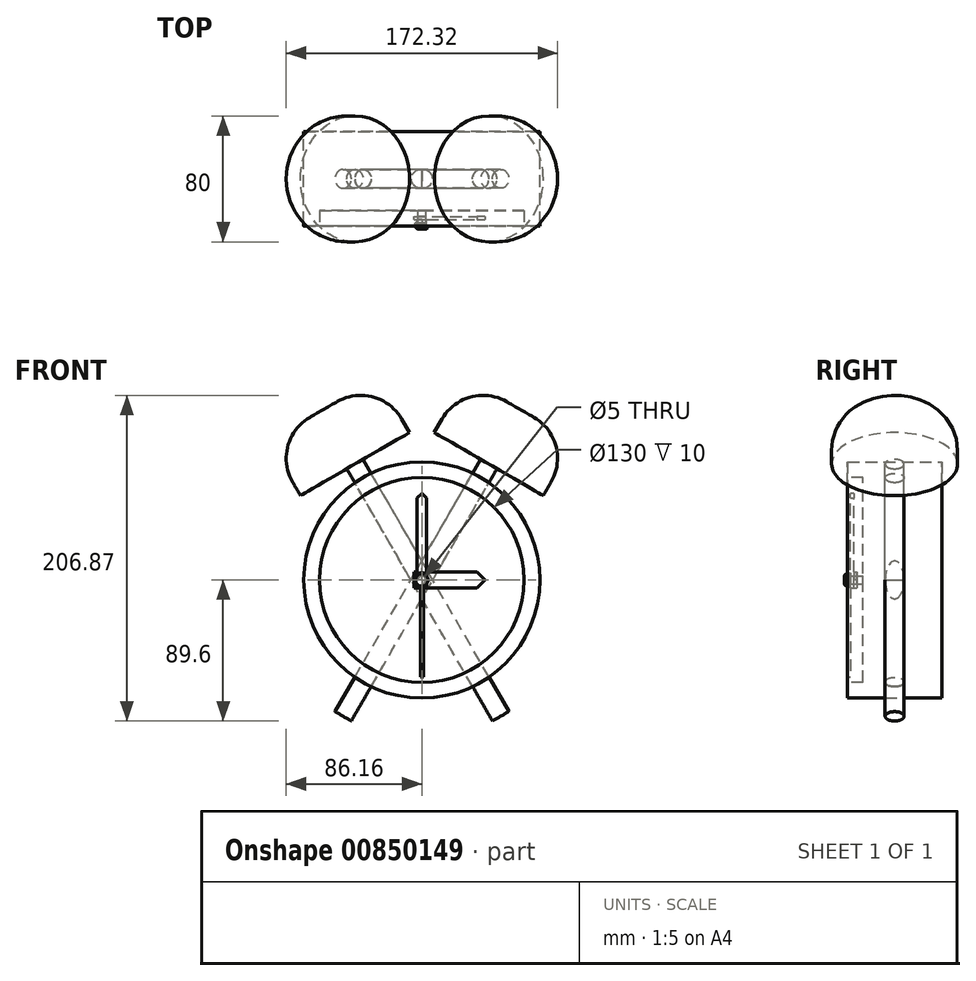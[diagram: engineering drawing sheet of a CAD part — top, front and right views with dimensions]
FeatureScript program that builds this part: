
annotation { "Feature Type Name" : "Feature", "Feature Type Description" : "" }
export const myFeature = defineFeature(function(context is Context, id is Id, definition is map)
    precondition{}
    {
        {
            var Q0;
            Q0=qCreatedBy(makeId("Front.planeOp"),FACE);
            var sketch = newSketch(context, id + "F0", { "sketchPlane" : qUnion([Q0])});
            skCircle(sketch, "E0", {"center": v(0, 0) * mm, "radius": 75 * mm});
            skSolve(sketch);
        }
        {
            var Q0;
            Q0=makeQuery(id+"F0.imprint","IMPRINT",FACE,{"disambiguationData":[TD([[makeQuery(id+"F0.imprint","IMPRINT",EDGE,{"derivedFrom":sQuery(id+"F0.wireOp",EDGE,"E0")}),1.0]])]});
            extrude(context, id + "F1", {"entities" : qUnion([Q0]), "depth" : 60 * mm, "offsetDistance" : 25 * mm});
        }
        {
            var Q0;
            Q0=makeQuery(id+"F1.opExtrude","CAP_FACE",FACE,{"disambiguationData":[OSD([sQuery(id+"F0.wireOp",EDGE,"E0")])],"isStart":false});
            var sketch = newSketch(context, id + "F2", { "sketchPlane" : qUnion([Q0])});
            skCircle(sketch, "E1", {"center": v(0, 0) * mm, "radius": 65 * mm});
            skSolve(sketch);
        }
        {
            var Q0;
            Q0=makeQuery(id+"F2.imprint","IMPRINT",FACE,{"disambiguationData":[TD([[makeQuery(id+"F2.imprint","IMPRINT",EDGE,{"derivedFrom":sQuery(id+"F2.wireOp",EDGE,"E1")}),1.0]])]});
            extrude(context, id + "F3", {"entities" : qUnion([Q0]), "operationType" : NewBodyOperationType.REMOVE, "oppositeDirection" : true, "depth" : 10 * mm, "offsetDistance" : 25 * mm});
        }
        {
            var Q0;
            Q0=qCreatedBy(makeId("Front.planeOp"),FACE);
            var sketch = newSketch(context, id + "F4", { "sketchPlane" : qUnion([Q0])});
            skLineSegment(sketch, "E2", {"start": v(0, 125) * mm, "end": v(0, -100) * mm});
            skLineSegment(sketch, "E3", {"start": v(0, 125) * mm, "end": v(40, 125) * mm});
            skLineSegment(sketch, "E4", {"start": v(6, -100) * mm, "end": v(0, -100) * mm});
            skLineSegment(sketch, "E5", {"start": v(40, 125) * mm, "end": v(40, 85) * mm});
            skLineSegment(sketch, "E6", {"start": v(40, 85) * mm, "end": v(6, 85) * mm});
            skLineSegment(sketch, "E7", {"start": v(6, -100) * mm, "end": v(6, 85) * mm});
            skSolve(sketch);
        }
        {
            var Q0;
            Q0 = qSketchRegion(id + "F4", true);
            var Q1;
            Q1=sQuery(id+"F4.wireOp",EDGE,"E2");
            revolve(context, id + "F5", {"surfaceOperationType" : NewSurfaceOperationType.NEW, "entities" : qUnion([Q0]), "axis" : qUnion([Q1]), "revolveType" : RevolveType.FULL});
        }
        {
            var Q0;
            Q0=makeQuery(id+"F5.opRevolve","SWEPT_EDGE",EDGE,{"disambiguationData":[OSD([sQuery(id+"F4.wireOp",EDGE,"E3"),sQuery(id+"F4.wireOp",EDGE,"E5")])]});
            fillet(context, id + "F6", {"entities" : qUnion([Q0]), "radius" : 30 * mm, "tangentPropagation" : true, "allowEdgeOverflow" : false});
        }
        {
            var Q0;
            Q0=makeQuery(id+"F5.opRevolve","SWEPT_BODY",BODY,{"disambiguationData":[OSD([sQuery(id+"F4.wireOp",EDGE,"E2"),sQuery(id+"F4.wireOp",EDGE,"E3"),sQuery(id+"F4.wireOp",EDGE,"E4"),sQuery(id+"F4.wireOp",EDGE,"E5"),sQuery(id+"F4.wireOp",EDGE,"E6"),sQuery(id+"F4.wireOp",EDGE,"E7")])]});
            var Q1;
            Q1=sQuery(id+"F0.wireOp",EDGE,"E0");
            transform(context, id + "F7", {"entities" : qUnion([Q0]), "transformType" : TransformType.ROTATION, "transformAxis" : qUnion([Q1]), "angle" : 30 * degree, "oppositeDirection" : true, "makeCopy" : false});
        }
        {
            var Q0;
            Q0=makeQuery(id+"F5.opRevolve","SWEPT_BODY",BODY,{"disambiguationData":[OSD([sQuery(id+"F4.wireOp",EDGE,"E2"),sQuery(id+"F4.wireOp",EDGE,"E3"),sQuery(id+"F4.wireOp",EDGE,"E4"),sQuery(id+"F4.wireOp",EDGE,"E5"),sQuery(id+"F4.wireOp",EDGE,"E6"),sQuery(id+"F4.wireOp",EDGE,"E7")])]});
            transform(context, id + "F8", {"entities" : qUnion([Q0]), "transformType" : TransformType.TRANSLATION_3D, "dx" : 0 * mm, "dy" : -30 * mm, "dz" : 0 * mm, "makeCopy" : false});
        }
        {
            var Q0;
            Q0=makeQuery(id+"F5.opRevolve","SWEPT_BODY",BODY,{"disambiguationData":[OSD([sQuery(id+"F4.wireOp",EDGE,"E2"),sQuery(id+"F4.wireOp",EDGE,"E3"),sQuery(id+"F4.wireOp",EDGE,"E4"),sQuery(id+"F4.wireOp",EDGE,"E5"),sQuery(id+"F4.wireOp",EDGE,"E6"),sQuery(id+"F4.wireOp",EDGE,"E7")])]});
            var Q1;
            Q1=qCreatedBy(makeId("Right.planeOp"),FACE);
            mirror(context, id + "F9", {"entities" : qUnion([Q0]), "mirrorPlane" : qUnion([Q1])});
        }
        {
            var Q0;
            Q0=makeQuery(id+"F5.opRevolve","SWEPT_BODY",BODY,{"disambiguationData":[OSD([sQuery(id+"F4.wireOp",EDGE,"E2"),sQuery(id+"F4.wireOp",EDGE,"E3"),sQuery(id+"F4.wireOp",EDGE,"E4"),sQuery(id+"F4.wireOp",EDGE,"E5"),sQuery(id+"F4.wireOp",EDGE,"E6"),sQuery(id+"F4.wireOp",EDGE,"E7")])]});
            var Q1;
            Q1=makeQuery(id+"F9.opPattern","COPY",BODY,{"derivedFrom":makeQuery(id+"F5.opRevolve","SWEPT_BODY",BODY,{"disambiguationData":[OSD([sQuery(id+"F4.wireOp",EDGE,"E2"),sQuery(id+"F4.wireOp",EDGE,"E3"),sQuery(id+"F4.wireOp",EDGE,"E4"),sQuery(id+"F4.wireOp",EDGE,"E5"),sQuery(id+"F4.wireOp",EDGE,"E6"),sQuery(id+"F4.wireOp",EDGE,"E7")])]}),"instanceName":"1"});
            var Q2;
            Q2=makeQuery(id+"F1.opExtrude","SWEPT_BODY",BODY,{"disambiguationData":[OSD([sQuery(id+"F0.wireOp",EDGE,"E0")])]});
            booleanBodies(context, id + "F10", {"operationType" : BooleanOperationType.SUBTRACTION, "tools" : qUnion([Q0, Q1]), "targets" : qUnion([Q2]), "keepTools" : true});
        }
        {
            var Q0;
            Q0=makeQuery(id+"F3.boolean.opBoolean","COPY",FACE,{"derivedFrom":makeQuery(id+"F3.opExtrude","CAP_FACE",FACE,{"disambiguationData":[OSD([sQuery(id+"F2.wireOp",EDGE,"E1")])],"isStart":false})});
            var sketch = newSketch(context, id + "F11", { "sketchPlane" : qUnion([Q0])});
            skCircle(sketch, "E8", {"center": v(0, 0) * mm, "radius": 2.5 * mm});
            skSolve(sketch);
        }
        {
            var Q0;
            Q0=makeQuery(id+"F11.imprint","IMPRINT",FACE,{"disambiguationData":[TD([[makeQuery(id+"F11.imprint","IMPRINT",EDGE,{"derivedFrom":sQuery(id+"F11.wireOp",EDGE,"E8")}),1.0]])]});
            var Q1;
            Q1=sQuery(id+"F11.wireOp",EDGE,"E8");
            extrude(context, id + "F12", {"entities" : qUnion([Q0]), "operationType" : NewBodyOperationType.ADD, "surfaceEntities" : qUnion([Q1]), "depth" : 4 * mm, "offsetDistance" : 25 * mm});
        }
        {
            var Q0;
            Q0=makeQuery(id+"F12.opExtrude","CAP_FACE",FACE,{"disambiguationData":[OSD([sQuery(id+"F11.wireOp",EDGE,"E8")])],"isStart":false});
            var sketch = newSketch(context, id + "F13", { "sketchPlane" : qUnion([Q0])});
            skLineSegment(sketch, "E9.bottom", {"start": v(-5, 5) * mm, "end": v(40, 5) * mm});
            skLineSegment(sketch, "E9.top", {"start": v(-5, -5) * mm, "end": v(40, -5) * mm});
            skLineSegment(sketch, "E9.left", {"start": v(-5, 5) * mm, "end": v(-5, -5) * mm});
            skLineSegment(sketch, "E9.right", {"start": v(40, 5) * mm, "end": v(40, -5) * mm});
            skLineSegment(sketch, "E10", {"start": v(0, 0) * mm, "end": v(-5, 0) * mm});
            skSolve(sketch);
        }
        {
            var Q0;
            {var subQ3=sQuery(id+"F13.wireOp",EDGE,"E9.bottom");Q0=makeQuery(id+"F13.imprint","IMPRINT",FACE,{"disambiguationData":[TD([[makeQuery(id+"F13.imprint","IMPRINT",EDGE,{"derivedFrom":subQ3}),-1.0]])]});}
            extrude(context, id + "F14", {"entities" : qUnion([Q0]), "depth" : 2 * mm, "offsetDistance" : 25 * mm});
        }
        {
            var Q0;
            Q0=makeQuery(id+"F14.opExtrude","SWEPT_EDGE",EDGE,{"disambiguationData":[OSD([sQuery(id+"F13.wireOp",EDGE,"E9.bottom"),sQuery(id+"F13.wireOp",EDGE,"E9.right")])]});
            var Q1;
            Q1=makeQuery(id+"F14.opExtrude","SWEPT_EDGE",EDGE,{"disambiguationData":[OSD([sQuery(id+"F13.wireOp",EDGE,"E9.top"),sQuery(id+"F13.wireOp",EDGE,"E9.right")])]});
            chamfer(context, id + "F15", {"entities" : qUnion([Q0, Q1]), "width" : 5 * mm, "tangentPropagation" : true});
        }
        {
            var Q0;
            Q0=makeQuery(id+"F14.opExtrude","CAP_FACE",FACE,{"disambiguationData":[OSD([sQuery(id+"F11.wireOp",EDGE,"E8"),sQuery(id+"F13.wireOp",EDGE,"E9.bottom"),sQuery(id+"F13.wireOp",EDGE,"E9.top"),sQuery(id+"F13.wireOp",EDGE,"E9.left"),sQuery(id+"F13.wireOp",EDGE,"E9.right")])],"isStart":false});
            var sketch = newSketch(context, id + "F16", { "sketchPlane" : qUnion([Q0])});
            skLineSegment(sketch, "E11.bottom", {"start": v(-3, -5) * mm, "end": v(3, -5) * mm});
            skLineSegment(sketch, "E11.top", {"start": v(-3, 55) * mm, "end": v(3, 55) * mm});
            skLineSegment(sketch, "E11.left", {"start": v(-3, -5) * mm, "end": v(-3, 55) * mm});
            skLineSegment(sketch, "E11.right", {"start": v(3, -5) * mm, "end": v(3, 55) * mm});
            skLineSegment(sketch, "E12", {"start": v(0, 0) * mm, "end": v(0, -5) * mm});
            skSolve(sketch);
        }
        {
            var Q0;
            {var subQ0=sQuery(id+"F16.wireOp",EDGE,"E11.top");Q0=makeQuery(id+"F16.imprint","IMPRINT",FACE,{"disambiguationData":[TD([[makeQuery(id+"F16.imprint","IMPRINT",EDGE,{"derivedFrom":subQ0}),-1.0]])]});}
            var Q1;
            Q1=makeQuery(id+"F16.imprint","IMPRINT",FACE,{"disambiguationData":[TD([[makeQuery(id+"F16.imprint","IMPRINT",EDGE,{"derivedFrom":makeQuery(id+"F14.opExtrude","CAP_EDGE",EDGE,{"disambiguationData":[OSD([sQuery(id+"F11.wireOp",EDGE,"E8")])],"isStart":false})}),-1.0]])]});
            extrude(context, id + "F17", {"entities" : qUnion([Q0, Q1]), "operationType" : NewBodyOperationType.ADD, "depth" : 2 * mm, "offsetDistance" : 25 * mm});
        }
        {
            var Q0;
            Q0=makeQuery(id+"F17.opExtrude","SWEPT_EDGE",EDGE,{"disambiguationData":[OSD([sQuery(id+"F16.wireOp",EDGE,"E11.top"),sQuery(id+"F16.wireOp",EDGE,"E11.right")])]});
            var Q1;
            Q1=makeQuery(id+"F17.opExtrude","SWEPT_EDGE",EDGE,{"disambiguationData":[OSD([sQuery(id+"F16.wireOp",EDGE,"E11.top"),sQuery(id+"F16.wireOp",EDGE,"E11.left")])]});
            chamfer(context, id + "F18", {"entities" : qUnion([Q0, Q1]), "width" : 3 * mm, "tangentPropagation" : true});
        }
        {
            var Q0;
            Q0=makeQuery(id+"F17.opExtrude","CAP_FACE",FACE,{"disambiguationData":[OSD([sQuery(id+"F11.wireOp",EDGE,"E8"),sQuery(id+"F16.wireOp",EDGE,"E11.bottom"),sQuery(id+"F16.wireOp",EDGE,"E11.top"),sQuery(id+"F16.wireOp",EDGE,"E11.left"),sQuery(id+"F16.wireOp",EDGE,"E11.right")])],"isStart":false});
            var sketch = newSketch(context, id + "F19", { "sketchPlane" : qUnion([Q0])});
            skCircle(sketch, "E13", {"center": v(0, 0) * mm, "radius": 4.5 * mm});
            skLineSegment(sketch, "E14.bottom", {"start": v(-1, -1.5) * mm, "end": v(1, -1.5) * mm});
            skLineSegment(sketch, "E14.top", {"start": v(-1, -61.5) * mm, "end": v(1, -61.5) * mm});
            skLineSegment(sketch, "E14.left", {"start": v(1, -1.5) * mm, "end": v(1, -61.5) * mm});
            skLineSegment(sketch, "E14.right", {"start": v(-1, -1.5) * mm, "end": v(-1, -61.5) * mm});
            skLineSegment(sketch, "E15", {"start": v(0, -1.5) * mm, "end": v(0, 0) * mm});
            skSolve(sketch);
        }
        {
            var Q0;
            {var subQ1=sQuery(id+"F19.wireOp",EDGE,"E13");var subQ7=makeQuery(id+"F17.opExtrude","CAP_EDGE",EDGE,{"disambiguationData":[OSD([sQuery(id+"F16.wireOp",EDGE,"E11.left")])],"isStart":false});var subQ9=makeQuery(id+"F19.imprint","INTERSECT",VERTEX,{"disambiguationData":[OD(0.0)],"derivedFrom":[subQ7,subQ1]});Q0=makeQuery(id+"F19.imprint","IMPRINT",FACE,{"disambiguationData":[TD([[makeQuery(id+"F19.imprint","IMPRINT",EDGE,{"disambiguationData":[TD([[subQ9,1.0]])],"derivedFrom":subQ1}),1.0]])]});}
            var Q1;
            {var subQ0=sQuery(id+"F19.wireOp",EDGE,"E13");var subQ1=makeQuery(id+"F17.opExtrude","CAP_EDGE",EDGE,{"disambiguationData":[OSD([sQuery(id+"F16.wireOp",EDGE,"E11.right")])],"isStart":false});var subQ2=makeQuery(id+"F19.imprint","INTERSECT",VERTEX,{"disambiguationData":[OD(0.0)],"derivedFrom":[subQ1,subQ0]});Q1=makeQuery(id+"F19.imprint","IMPRINT",FACE,{"disambiguationData":[TD([[makeQuery(id+"F19.imprint","IMPRINT",EDGE,{"disambiguationData":[TD([[subQ2,1.0]])],"derivedFrom":subQ0}),1.0]])]});}
            var Q2;
            {var subQ0=sQuery(id+"F19.wireOp",EDGE,"E13");var subQ1=makeQuery(id+"F17.opExtrude","CAP_EDGE",EDGE,{"disambiguationData":[OSD([sQuery(id+"F16.wireOp",EDGE,"E11.left")])],"isStart":false});var subQ2=makeQuery(id+"F19.imprint","INTERSECT",VERTEX,{"disambiguationData":[OD(0.0)],"derivedFrom":[subQ1,subQ0]});Q2=makeQuery(id+"F19.imprint","IMPRINT",FACE,{"disambiguationData":[TD([[makeQuery(id+"F19.imprint","IMPRINT",EDGE,{"disambiguationData":[TD([[subQ2,-1.0]])],"derivedFrom":subQ0}),1.0]])]});}
            var Q3;
            {var subQ0=sQuery(id+"F19.wireOp",EDGE,"E14.right");var subQ1=sQuery(id+"F19.wireOp",EDGE,"E13");var subQ2=makeQuery(id+"F19.imprint","INTERSECT",VERTEX,{"derivedFrom":[subQ1,subQ0]});Q3=makeQuery(id+"F19.imprint","IMPRINT",FACE,{"disambiguationData":[TD([[makeQuery(id+"F19.imprint","IMPRINT",EDGE,{"disambiguationData":[TD([[subQ2,-1.0]])],"derivedFrom":subQ1}),1.0]])]});}
            var Q4;
            {var subQ0=sQuery(id+"F19.wireOp",EDGE,"E14.top");Q4=makeQuery(id+"F19.imprint","IMPRINT",FACE,{"disambiguationData":[TD([[makeQuery(id+"F19.imprint","IMPRINT",EDGE,{"derivedFrom":subQ0}),1.0]])]});}
            var Q5;
            {var subQ0=sQuery(id+"F19.wireOp",EDGE,"E14.right");var subQ1=sQuery(id+"F19.wireOp",EDGE,"E13");var subQ2=makeQuery(id+"F19.imprint","INTERSECT",VERTEX,{"derivedFrom":[subQ1,subQ0]});Q5=makeQuery(id+"F19.imprint","IMPRINT",FACE,{"disambiguationData":[TD([[makeQuery(id+"F19.imprint","IMPRINT",EDGE,{"disambiguationData":[TD([[subQ2,-1.0]])],"derivedFrom":subQ1}),-1.0]])]});}
            extrude(context, id + "F20", {"entities" : qUnion([Q0, Q1, Q2, Q3, Q4, Q5]), "depth" : 2 * mm, "offsetDistance" : 25 * mm});
        }
        {
            var Q0;
            Q0=makeQuery(id+"F12.opExtrude","CAP_FACE",FACE,{"disambiguationData":[OSD([sQuery(id+"F11.wireOp",EDGE,"E8")])],"isStart":false});
            var Q1;
            Q1=makeQuery(id+"F20.opExtrude","CAP_FACE",FACE,{"disambiguationData":[OSD([sQuery(id+"F11.wireOp",EDGE,"E8"),sQuery(id+"F19.wireOp",EDGE,"E13"),sQuery(id+"F19.wireOp",EDGE,"E14.top"),sQuery(id+"F19.wireOp",EDGE,"E14.left"),sQuery(id+"F19.wireOp",EDGE,"E14.right")])],"isStart":false});
            extrude(context, id + "F21", {"entities" : qUnion([Q0]), "endBound" : BoundingType.UP_TO_SURFACE, "depth" : 25 * mm, "endBoundEntityFace" : qUnion([Q1]), "offsetDistance" : 25 * mm});
        }
        {
            var Q0;
            Q0=makeQuery(id+"F21.opExtrude","CAP_FACE",FACE,{"disambiguationData":[OSD([sQuery(id+"F11.wireOp",EDGE,"E8")])],"isStart":false});
            var sketch = newSketch(context, id + "F22", { "sketchPlane" : qUnion([Q0])});
            skCircle(sketch, "E16", {"center": v(0, 0) * mm, "radius": 4 * mm});
            skSolve(sketch);
        }
        {
            var Q0;
            Q0=makeQuery(id+"F22.imprint","IMPRINT",FACE,{"disambiguationData":[TD([[makeQuery(id+"F22.imprint","IMPRINT",EDGE,{"derivedFrom":sQuery(id+"F22.wireOp",EDGE,"E16")}),1.0]])]});
            var Q1;
            Q1=makeQuery(id+"F22.imprint","IMPRINT",FACE,{"disambiguationData":[TD([[makeQuery(id+"F22.imprint","IMPRINT",EDGE,{"derivedFrom":makeQuery(id+"F21.opExtrude","CAP_EDGE",EDGE,{"disambiguationData":[OSD([sQuery(id+"F11.wireOp",EDGE,"E8")])],"isStart":false})}),1.0]])]});
            extrude(context, id + "F23", {"entities" : qUnion([Q0, Q1]), "operationType" : NewBodyOperationType.ADD, "depth" : 2 * mm, "offsetDistance" : 25 * mm});
        }
        {
            var Q0;
            Q0=makeQuery(id+"F23.opExtrude","CAP_EDGE",EDGE,{"disambiguationData":[OSD([sQuery(id+"F22.wireOp",EDGE,"E16")])],"isStart":false});
            fillet(context, id + "F24", {"entities" : qUnion([Q0]), "radius" : 2 * mm, "tangentPropagation" : true, "allowEdgeOverflow" : false});
        }
    });
